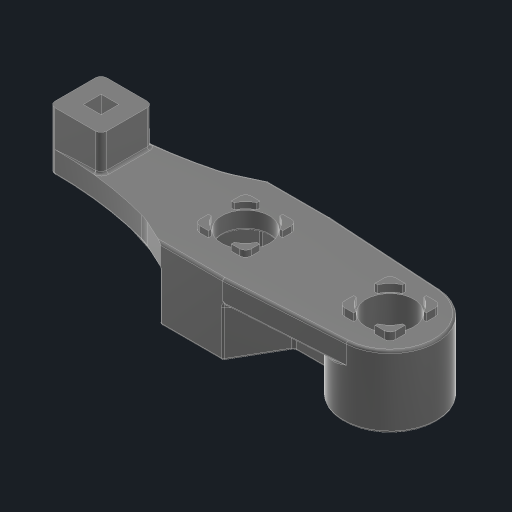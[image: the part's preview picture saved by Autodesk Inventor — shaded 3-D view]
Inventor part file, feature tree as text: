
AUTODESK INVENTOR PART (.ipt)
format: ipt  version: 2023 (Build 270158030, 158C)  size: 507,392 bytes
history: native  units: in
note: dims shown in document units (in); Inventor stores cm internally (conversion verified against a paired STEP export)
features: extrude x1, sketch x1, fillet x1
ambient origin geometry x8: Origin, YZ Plane, XZ Plane, XY Plane, X Axis, Y Axis, Z Axis, Center Point
bodies: Solid1 (feature_tree)
feature tree (3):
  extrude  "Extrusion1"  [1 undecoded]
  sketch  "Sketch1"  dims[d0=0.3937in d1=0.0in]
  fillet  "Fillet18"  [1 undecoded]
note: 2 required parameter values undecoded (feature->parameter linkage not recoverable at this tier; creation-order binding heuristic only, values carry confidence <= 0.55)
